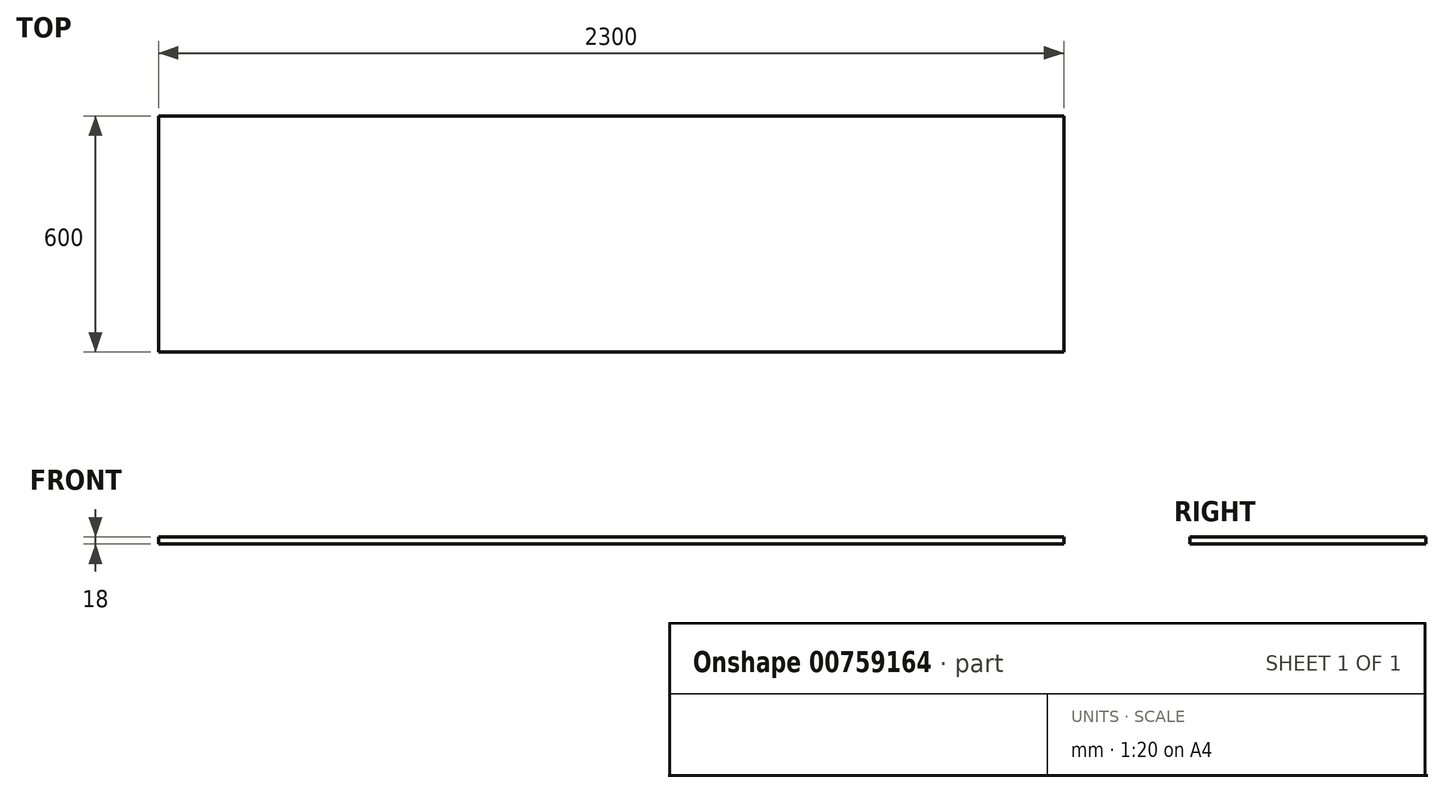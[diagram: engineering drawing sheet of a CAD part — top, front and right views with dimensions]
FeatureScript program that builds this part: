
annotation { "Feature Type Name" : "Feature", "Feature Type Description" : "" }
export const myFeature = defineFeature(function(context is Context, id is Id, definition is map)
    precondition{}
    {
        {
            var Q0;
            Q0=qCreatedBy(makeId("Top.planeOp"),FACE);
            var sketch = newSketch(context, id + "F0", { "sketchPlane" : qUnion([Q0])});
            skLineSegment(sketch, "E0.bottom", {"start": v(1150, -300) * mm, "end": v(-1150, -300) * mm});
            skLineSegment(sketch, "E0.top", {"start": v(1150, 300) * mm, "end": v(-1150, 300) * mm});
            skLineSegment(sketch, "E0.left", {"start": v(1150, -300) * mm, "end": v(1150, 300) * mm});
            skLineSegment(sketch, "E0.right", {"start": v(-1150, -300) * mm, "end": v(-1150, 300) * mm});
            skPoint(sketch, "E0.middle", {"position": v(0, 0) * mm});
            skSolve(sketch);
        }
        {
            var Q0;
            Q0=qSketchRegion(id+"F0",true);
            extrude(context, id + "F1", {"entities" : qUnion([Q0]), "depth" : 18 * mm, "offsetDistance" : 25 * mm});
        }
    });
